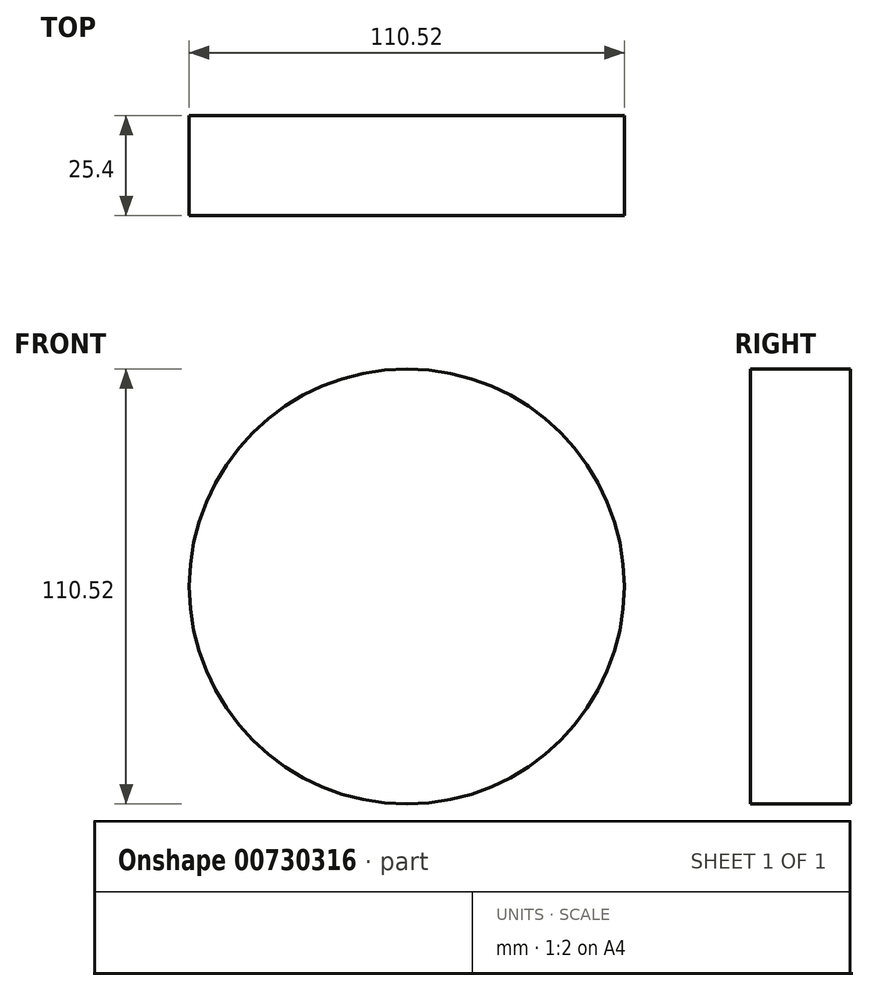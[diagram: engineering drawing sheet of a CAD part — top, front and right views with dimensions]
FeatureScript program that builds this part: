
annotation { "Feature Type Name" : "Feature", "Feature Type Description" : "" }
export const myFeature = defineFeature(function(context is Context, id is Id, definition is map)
    precondition{}
    {
        {
            var Q0;
            Q0=qCreatedBy(makeId("Front.planeOp"),FACE);
            var sketch = newSketch(context, id + "F0", { "sketchPlane" : qUnion([Q0])});
            skCircle(sketch, "E0", {"center": v(15.36, 53.08) * mm, "radius": 55.26 * mm});
            skSolve(sketch);
        }
        {
            var Q0;
            Q0 = qSketchRegion(id + "F0", true);
            extrude(context, id + "F1", {"entities" : qUnion([Q0]), "depth" : 25.4 * mm, "offsetDistance" : 25.4 * mm});
        }
    });
